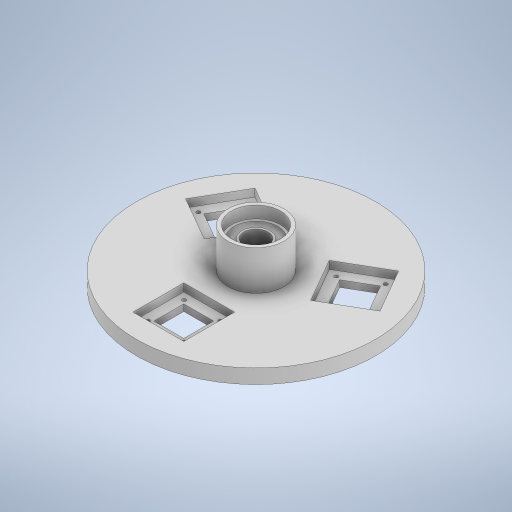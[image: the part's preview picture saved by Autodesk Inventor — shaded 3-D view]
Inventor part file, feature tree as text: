
AUTODESK INVENTOR PART (.ipt)
format: ipt  version: 2024 (Build 280153000, 153)  size: 344,576 bytes
history: native  units: mm
features: sketch x8, extrude x6, pattern_circular x3, revolve x2, projected_geometry x1
ambient origin geometry x8: Origin, YZ Plane, XZ Plane, XY Plane, X Axis, Y Axis, Z Axis, Center Point
bodies: Solid1 (feature_tree)
feature tree (20):
  extrude  "Extrusion1"  Depth=12.0mm TaperAngle=0.0deg
  extrude  "Extrusion2"  Depth=33.0mm TaperAngle=0.0deg
  extrude  "Extrusion7"  Depth=35.0mm
  revolve  "Revolution1"  [1 undecoded]
  revolve  "Revolution2"  [1 undecoded]
  extrude  "Extrusion8"  Depth=6.35mm
  pattern_circular  "Circular Pattern2"  [2 undecoded]
  extrude  "Extrusion9"  Depth=25.0mm
  pattern_circular  "Circular Pattern3"  [2 undecoded]
  extrude  "Extrusion10"  Depth=25.0mm
  pattern_circular  "Circular Pattern4"  [2 undecoded]
  sketch  "Sketch1"  dims[d0=200.0mm d1=12.0mm d2=0.0mm]
  sketch  "Sketch2"  dims[d3=47.0mm d4=33.0mm d5=0.0mm]
  sketch  "Sketch7"  dims[d33=3.0mm d37=35.0mm]
  projected_geometry  "Projected Loop2"
  sketch  "Sketch8"  dims[d38=23.0mm d39=0.0mm d40=20.0mm]
  sketch  "Sketch9"  dims[d41=6.35mm d42=5.0mm]
  sketch  "Sketch10"  dims[d43=90.0deg d44=6.35mm]
  sketch  "Sketch11"  dims[d45=15.0mm]
  sketch  "Sketch12"  dims[d46=360.0deg d47=30.4mm d48=30.4mm d49=3.2mm d50=20.0mm d52=30.4mm d53=20.0mm d55=30.4mm d58=45.0mm d59=0.0mm d60=0.0mm d61=30.0mm d62=360.0deg d64=42.5mm d65=42.5mm d66=39.2mm d67=6.5mm d68=0.0mm d69=30.0mm d70=360.0deg d72=25.0mm d73=25.0mm d74=0.0mm d75=0.0mm d76=30.0mm d77=360.0deg]
note: 8 required parameter values undecoded (feature->parameter linkage not recoverable at this tier; creation-order binding heuristic only, values carry confidence <= 0.55)